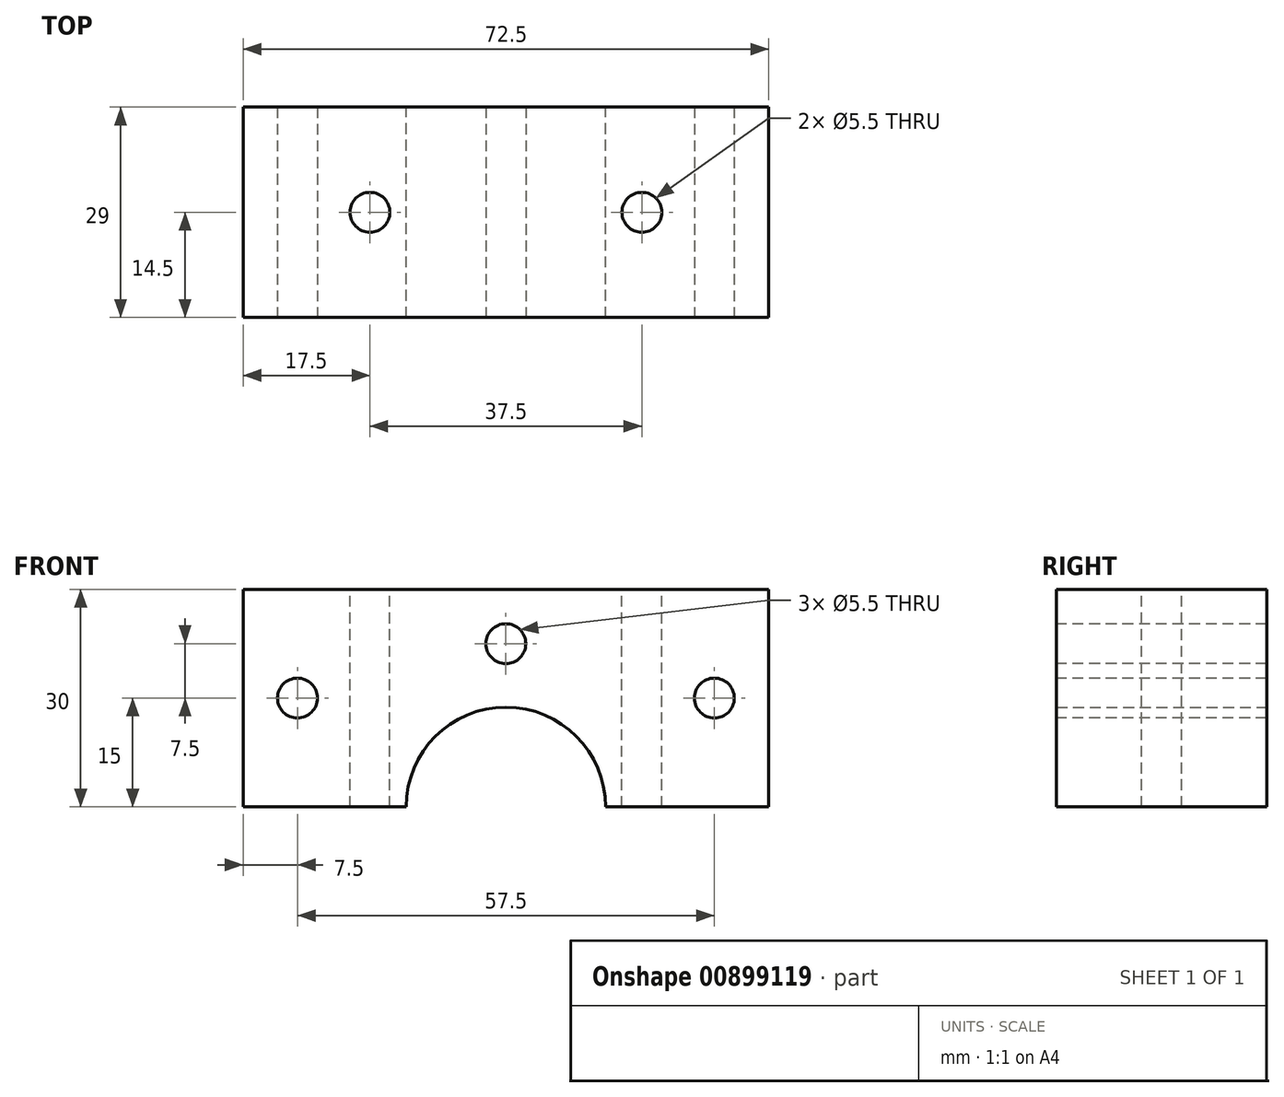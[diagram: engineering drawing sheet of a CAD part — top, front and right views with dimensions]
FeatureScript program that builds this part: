
annotation { "Feature Type Name" : "Feature", "Feature Type Description" : "" }
export const myFeature = defineFeature(function(context is Context, id is Id, definition is map)
    precondition{}
    {
        {
            var Q0;
            Q0=qCreatedBy(makeId("Front.planeOp"),FACE);
            var sketch = newSketch(context, id + "F0", { "sketchPlane" : qUnion([Q0])});
            skArc(sketch, "E0", {"start": v(13.75, 0) * mm, "mid": v(0, 13.75) * mm, "end": v(-13.75, 0) * mm});
            skLineSegment(sketch, "E1", {"start": v(-13.75, 0) * mm, "end": v(-36.25, 0) * mm});
            skLineSegment(sketch, "E2", {"start": v(-36.25, 0) * mm, "end": v(-36.25, 30) * mm});
            skLineSegment(sketch, "E3", {"start": v(-36.25, 30) * mm, "end": v(36.25, 30) * mm});
            skLineSegment(sketch, "E4", {"start": v(36.25, 30) * mm, "end": v(36.25, 0) * mm});
            skLineSegment(sketch, "E5", {"start": v(36.25, 0) * mm, "end": v(13.75, 0) * mm});
            skSolve(sketch);
        }
        {
            var Q0;
            Q0 = qSketchRegion(id + "F0", true);
            extrude(context, id + "F1", {"entities" : qUnion([Q0]), "depth" : 29 * mm, "offsetDistance" : 25 * mm});
        }
        {
            var Q0;
            Q0=makeQuery(id+"F1.opExtrude","SWEPT_FACE",FACE,{"disambiguationData":[OSD([sQuery(id+"F0.wireOp",EDGE,"E3")])]});
            var sketch = newSketch(context, id + "F2", { "sketchPlane" : qUnion([Q0])});
            skCircle(sketch, "E6", {"center": v(-18.75, -14.5) * mm, "radius": 2.75 * mm});
            skPoint(sketch, "E6.centerSnap0", {"position": v(-36.25, -14.5) * mm});
            skCircle(sketch, "E7", {"center": v(18.75, -14.5) * mm, "radius": 2.75 * mm});
            skPoint(sketch, "E7.centerSnap0", {"position": v(36.25, -14.5) * mm});
            skSolve(sketch);
        }
        {
            var Q0;
            Q0 = qSketchRegion(id + "F2", true);
            extrude(context, id + "F3", {"entities" : qUnion([Q0]), "operationType" : NewBodyOperationType.REMOVE, "oppositeDirection" : true, "depth" : 50 * mm, "offsetDistance" : 25 * mm});
        }
        {
            var Q0;
            Q0=makeQuery(id+"F1.opExtrude","CAP_FACE",FACE,{"disambiguationData":[OSD([sQuery(id+"F0.wireOp",EDGE,"E0"),sQuery(id+"F0.wireOp",EDGE,"E1"),sQuery(id+"F0.wireOp",EDGE,"E2"),sQuery(id+"F0.wireOp",EDGE,"E3"),sQuery(id+"F0.wireOp",EDGE,"E4"),sQuery(id+"F0.wireOp",EDGE,"E5")])],"isStart":false});
            var sketch = newSketch(context, id + "F4", { "sketchPlane" : qUnion([Q0])});
            skCircle(sketch, "E8", {"center": v(-28.75, 15) * mm, "radius": 2.75 * mm});
            skPoint(sketch, "E8.centerSnap0", {"position": v(-36.25, 15) * mm});
            skCircle(sketch, "E9", {"center": v(0, 22.5) * mm, "radius": 2.75 * mm});
            skPoint(sketch, "E9.centerSnap0", {"position": v(0, 30) * mm});
            skCircle(sketch, "E10", {"center": v(28.75, 15) * mm, "radius": 2.75 * mm});
            skPoint(sketch, "E10.centerSnap0", {"position": v(36.25, 15) * mm});
            skSolve(sketch);
        }
        {
            var Q0;
            Q0 = qSketchRegion(id + "F4", true);
            extrude(context, id + "F5", {"entities" : qUnion([Q0]), "operationType" : NewBodyOperationType.REMOVE, "oppositeDirection" : true, "depth" : 50 * mm, "offsetDistance" : 25 * mm});
        }
    });
